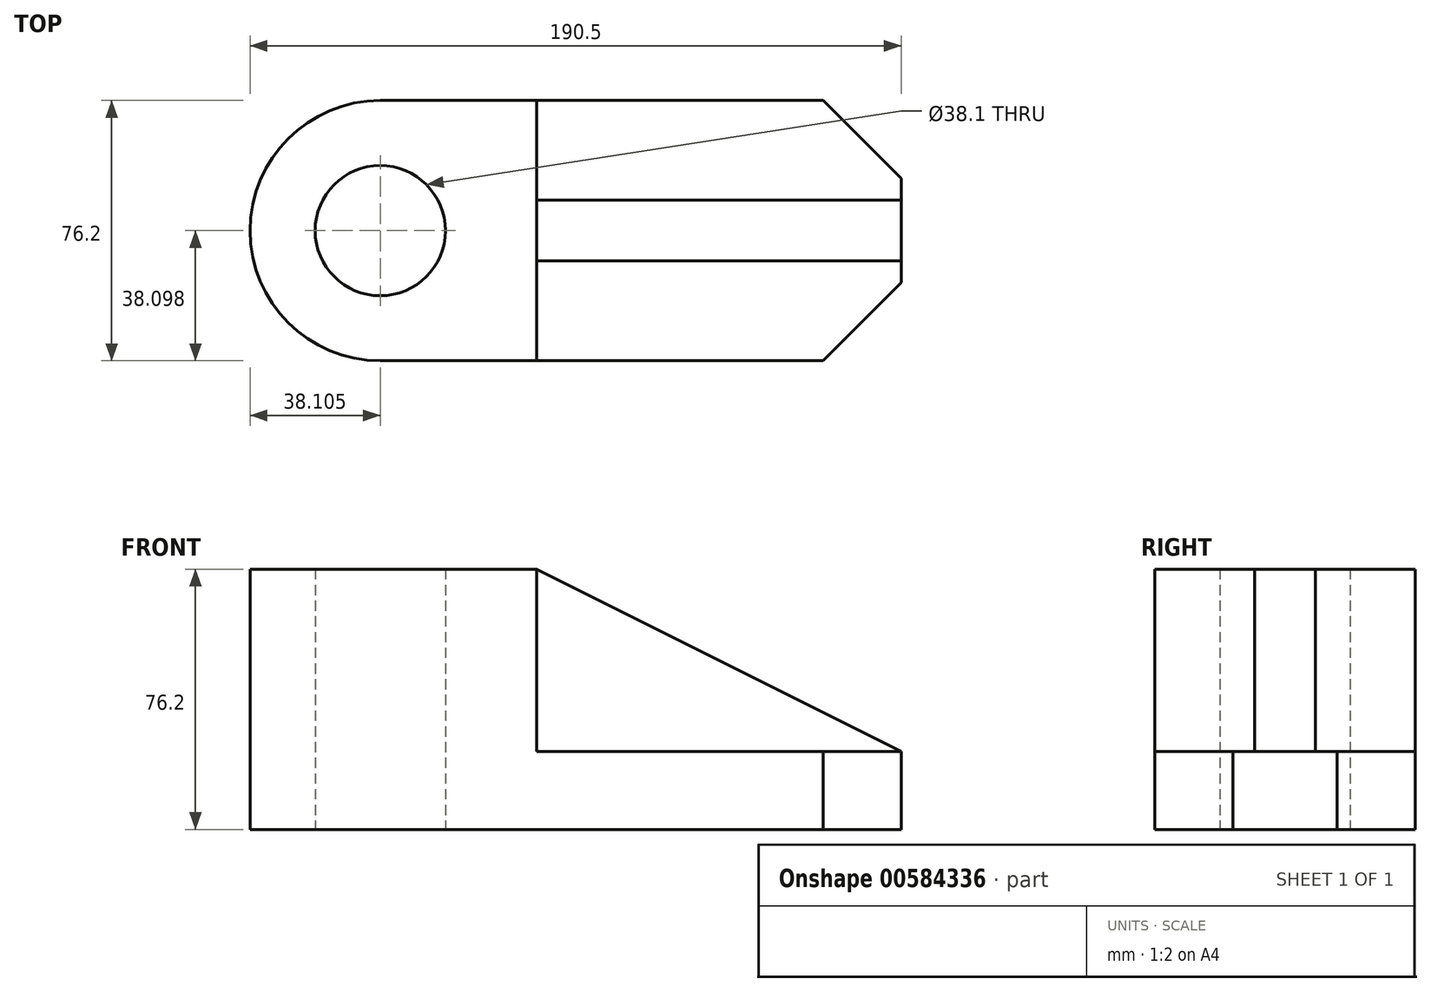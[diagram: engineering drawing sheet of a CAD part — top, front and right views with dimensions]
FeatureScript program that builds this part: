
annotation { "Feature Type Name" : "Feature", "Feature Type Description" : "" }
export const myFeature = defineFeature(function(context is Context, id is Id, definition is map)
    precondition{}
    {
        {
            var Q0;
            Q0=qCreatedBy(makeId("Top.planeOp"),FACE);
            var sketch = newSketch(context, id + "F0", { "sketchPlane" : qUnion([Q0])});
            skArc(sketch, "E0", {"start": v(-80.8, 36.94) * mm, "mid": v(-118.9, -1.16) * mm, "end": v(-80.8, -39.26) * mm});
            skCircle(sketch, "E1", {"center": v(-80.8, -1.16) * mm, "radius": 19.05 * mm});
            skLineSegment(sketch, "E2", {"start": v(-80.8, 36.94) * mm, "end": v(48.74, 36.94) * mm});
            skLineSegment(sketch, "E3", {"start": v(-80.8, -39.26) * mm, "end": v(48.74, -39.26) * mm});
            skLineSegment(sketch, "E4", {"start": v(71.6, 14.08) * mm, "end": v(71.6, -16.4) * mm});
            skLineSegment(sketch, "E5", {"start": v(-35.08, 36.94) * mm, "end": v(-35.08, -39.26) * mm});
            skLineSegment(sketch, "E6", {"start": v(48.74, 36.94) * mm, "end": v(71.6, 14.08) * mm});
            skLineSegment(sketch, "E7", {"start": v(71.6, -16.4) * mm, "end": v(48.74, -39.26) * mm});
            skLineSegment(sketch, "E8", {"start": v(71.6, 7.73) * mm, "end": v(-35.08, 7.73) * mm});
            skLineSegment(sketch, "E9", {"start": v(71.6, -10.05) * mm, "end": v(-35.08, -10.05) * mm});
            skPoint(sketch, "E10.orphan", {"position": v(71.6, 36.94) * mm});
            skPoint(sketch, "E11.orphan", {"position": v(71.6, -39.26) * mm});
            skSolve(sketch);
        }
        {
            var Q0;
            {var subQ1=sQuery(id+"F0.wireOp",EDGE,"E0");Q0=makeQuery(id+"F0.imprint","IMPRINT",FACE,{"disambiguationData":[TD([[makeQuery(id+"F0.imprint","IMPRINT",EDGE,{"derivedFrom":subQ1}),1.0]])]});}
            extrude(context, id + "F1", {"entities" : qUnion([Q0]), "depth" : 76.2 * mm, "offsetDistance" : 25.4 * mm});
        }
        {
            var Q0;
            {var subQ4=sQuery(id+"F0.wireOp",EDGE,"E7");Q0=makeQuery(id+"F0.imprint","IMPRINT",FACE,{"disambiguationData":[TD([[makeQuery(id+"F0.imprint","IMPRINT",EDGE,{"derivedFrom":subQ4}),-1.0]])]});}
            extrude(context, id + "F2", {"entities" : qUnion([Q0]), "operationType" : NewBodyOperationType.ADD, "depth" : 22.86 * mm, "offsetDistance" : 25.4 * mm});
        }
        {
            var Q0;
            {var subQ0=sQuery(id+"F0.wireOp",EDGE,"E6");Q0=makeQuery(id+"F0.imprint","IMPRINT",FACE,{"disambiguationData":[TD([[makeQuery(id+"F0.imprint","IMPRINT",EDGE,{"derivedFrom":subQ0}),-1.0]])]});}
            extrude(context, id + "F3", {"entities" : qUnion([Q0]), "operationType" : NewBodyOperationType.ADD, "depth" : 22.86 * mm, "offsetDistance" : 25.4 * mm});
        }
        {
            var Q0;
            {var subQ0=sQuery(id+"F0.wireOp",EDGE,"E8");Q0=makeQuery(id+"F0.imprint","IMPRINT",FACE,{"disambiguationData":[TD([[makeQuery(id+"F0.imprint","IMPRINT",EDGE,{"derivedFrom":subQ0}),1.0]])]});}
            extrude(context, id + "F4", {"entities" : qUnion([Q0]), "operationType" : NewBodyOperationType.ADD, "depth" : 76.2 * mm, "offsetDistance" : 25.4 * mm});
        }
        {
            var Q0;
            Q0=makeQuery(id+"F4.opExtrude","SWEPT_FACE",FACE,{"disambiguationData":[OSD([sQuery(id+"F0.wireOp",EDGE,"E9")])]});
            var sketch = newSketch(context, id + "F5", { "sketchPlane" : qUnion([Q0])});
            skLineSegment(sketch, "E12", {"start": v(-35.08, 76.2) * mm, "end": v(71.6, 22.86) * mm});
            skSolve(sketch);
        }
        {
            var Q0;
            Q0=makeQuery(id+"F5.imprint","IMPRINT",FACE,{"disambiguationData":[TD([[makeQuery(id+"F5.imprint","IMPRINT",EDGE,{"derivedFrom":sQuery(id+"F5.wireOp",EDGE,"E12")}),1.0]])]});
            extrude(context, id + "F6", {"entities" : qUnion([Q0]), "operationType" : NewBodyOperationType.REMOVE, "oppositeDirection" : true, "depth" : 25.4 * mm, "offsetDistance" : 25.4 * mm});
        }
    });
